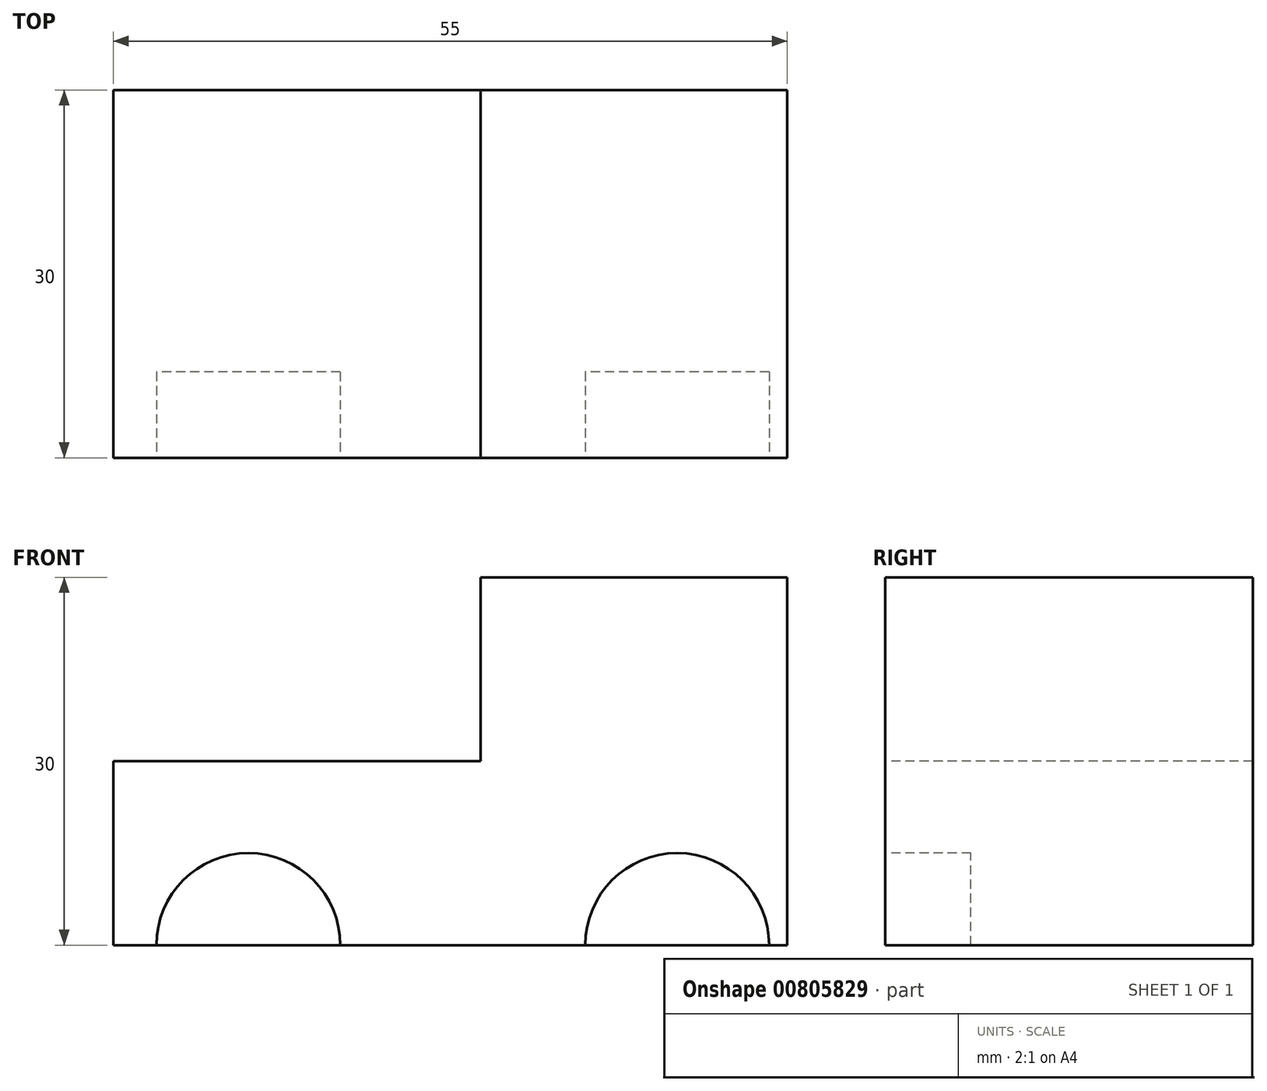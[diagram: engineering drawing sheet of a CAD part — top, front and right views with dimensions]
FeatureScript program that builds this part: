
annotation { "Feature Type Name" : "Feature", "Feature Type Description" : "" }
export const myFeature = defineFeature(function(context is Context, id is Id, definition is map)
    precondition{}
    {
        {
            var Q0;
            Q0=qCreatedBy(makeId("Front.planeOp"),FACE);
            var sketch = newSketch(context, id + "F0", { "sketchPlane" : qUnion([Q0])});
            skLineSegment(sketch, "E0.bottom", {"start": v(-3.96, -9.97) * mm, "end": v(-58.96, -9.97) * mm});
            skLineSegment(sketch, "E0.top", {"start": v(-3.96, -39.97) * mm, "end": v(-58.96, -39.97) * mm});
            skLineSegment(sketch, "E0.left", {"start": v(-3.96, -9.97) * mm, "end": v(-3.96, -39.97) * mm});
            skLineSegment(sketch, "E0.right", {"start": v(-58.96, -9.97) * mm, "end": v(-58.96, -39.97) * mm});
            skPoint(sketch, "E0.middle", {"position": v(-31.46, -24.97) * mm});
            skSolve(sketch);
        }
        {
            var Q0;
            Q0 = qSketchRegion(id + "F0", true);
            extrude(context, id + "F1", {"entities" : qUnion([Q0]), "depth" : 30 * mm, "offsetDistance" : 25 * mm});
        }
        {
            var Q0;
            Q0=makeQuery(id+"F1.opExtrude","CAP_FACE",FACE,{"disambiguationData":[OSD([sQuery(id+"F0.wireOp",EDGE,"E0.bottom"),sQuery(id+"F0.wireOp",EDGE,"E0.top"),sQuery(id+"F0.wireOp",EDGE,"E0.left"),sQuery(id+"F0.wireOp",EDGE,"E0.right")])],"isStart":false});
            var sketch = newSketch(context, id + "F2", { "sketchPlane" : qUnion([Q0])});
            skLineSegment(sketch, "E1", {"start": v(-58.96, -24.97) * mm, "end": v(-28.96, -24.97) * mm});
            skLineSegment(sketch, "E2", {"start": v(-28.96, -24.97) * mm, "end": v(-28.96, -9.97) * mm});
            skSolve(sketch);
        }
        {
            var Q0;
            {var subQ0=sQuery(id+"F2.wireOp",EDGE,"E1");Q0=makeQuery(id+"F2.imprint","IMPRINT",FACE,{"disambiguationData":[TD([[makeQuery(id+"F2.imprint","IMPRINT",EDGE,{"derivedFrom":subQ0}),1.0]])]});}
            extrude(context, id + "F3", {"entities" : qUnion([Q0]), "operationType" : NewBodyOperationType.REMOVE, "endBound" : BoundingType.THROUGH_ALL, "oppositeDirection" : true, "depth" : 25 * mm, "offsetDistance" : 25 * mm});
        }
        {
            var Q0;
            Q0=makeQuery(id+"F1.opExtrude","CAP_FACE",FACE,{"disambiguationData":[OSD([sQuery(id+"F0.wireOp",EDGE,"E0.bottom"),sQuery(id+"F0.wireOp",EDGE,"E0.top"),sQuery(id+"F0.wireOp",EDGE,"E0.left"),sQuery(id+"F0.wireOp",EDGE,"E0.right")])],"isStart":false});
            var sketch = newSketch(context, id + "F4", { "sketchPlane" : qUnion([Q0])});
            skCircle(sketch, "E3", {"center": v(-47.93, -39.97) * mm, "radius": 7.5 * mm});
            skCircle(sketch, "E4.1.0.0", {"center": v(-12.93, -39.97) * mm, "radius": 7.5 * mm});
            skLineSegment(sketch, "E4.direction1", {"start": v(-47.93, -39.97) * mm, "end": v(-12.93, -39.97) * mm, "construction": true});
            skSolve(sketch);
        }
        {
            var Q0;
            {var subQ0=sQuery(id+"F4.wireOp",EDGE,"E3");var subQ1=makeQuery(id+"F1.opExtrude","CAP_EDGE",EDGE,{"disambiguationData":[OSD([sQuery(id+"F0.wireOp",EDGE,"E0.top")])],"isStart":false});var subQ2=makeQuery(id+"F4.imprint","INTERSECT",VERTEX,{"disambiguationData":[OD(0.0)],"derivedFrom":[subQ1,subQ0]});Q0=makeQuery(id+"F4.imprint","IMPRINT",FACE,{"disambiguationData":[TD([[makeQuery(id+"F4.imprint","IMPRINT",EDGE,{"disambiguationData":[TD([[subQ2,1.0]])],"derivedFrom":subQ0}),1.0]])]});}
            var Q1;
            {var subQ0=sQuery(id+"F4.wireOp",EDGE,"E4.1.0.0");var subQ1=makeQuery(id+"F1.opExtrude","CAP_EDGE",EDGE,{"disambiguationData":[OSD([sQuery(id+"F0.wireOp",EDGE,"E0.top")])],"isStart":false});var subQ2=makeQuery(id+"F4.imprint","INTERSECT",VERTEX,{"disambiguationData":[OD(0.0)],"derivedFrom":[subQ1,subQ0]});Q1=makeQuery(id+"F4.imprint","IMPRINT",FACE,{"disambiguationData":[TD([[makeQuery(id+"F4.imprint","IMPRINT",EDGE,{"disambiguationData":[TD([[subQ2,-1.0]])],"derivedFrom":subQ0}),1.0]])]});}
            extrude(context, id + "F5", {"entities" : qUnion([Q0, Q1]), "operationType" : NewBodyOperationType.REMOVE, "oppositeDirection" : true, "depth" : 7 * mm, "offsetDistance" : 25 * mm});
        }
    });
